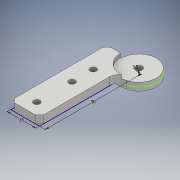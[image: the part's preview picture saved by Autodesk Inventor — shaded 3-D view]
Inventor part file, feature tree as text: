
AUTODESK INVENTOR PART (.ipt)
format: ipt  version: 2018.2 (Build 222227000, 227)  size: 151,552 bytes
history: native  units: mm
features: extrude x5, sketch x4, chamfer x3, fillet x1
ambient origin geometry x8: Origin, YZ Plane, XZ Plane, XY Plane, X Axis, Y Axis, Z Axis, Center Point
bodies: Solid1 (feature_tree)
feature tree (13):
  sketch  "Sketch1"  dims[d0=15.0mm d1=50.0mm d2=4.0mm d3=0.0mm]
  extrude  "Extrusion1"  Depth=50.0mm
  chamfer  "Chamfer2"  Distance=4.0mm
  extrude  "Extrusion2"  Depth=2.0mm
  extrude  "Extrusion3"  Depth=4.0mm
  chamfer  "Chamfer3"  Distance=4.0mm
  extrude  "Extrusion4"  Depth=2.0mm TaperAngle=45.0deg
  fillet  "Fillet1"  Radius=0.5mm
  chamfer  "Chamfer4"  Distance=10.0mm
  extrude  "Extrusion5"  Depth=5.0mm
  sketch  "Sketch2"  dims[d7=2.0mm d8=2.0mm d9=45.0deg d10=3.25mm]
  sketch  "Sketch3"  dims[d11=3.25mm d12=3.5mm d13=4.0mm d14=0.0mm]
  sketch  "Sketch4"  dims[d15=4.0mm d16=0.0mm d17=2.0mm d18=2.0mm d19=45.0deg d20=0.5mm d21=10.0mm d22=0.0mm d23=5.0mm d24=2.0mm d25=2.0mm d26=45.0deg d27=3.25mm d28=10.0mm d29=0.0mm]
